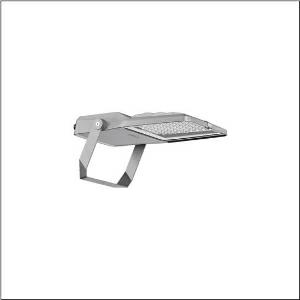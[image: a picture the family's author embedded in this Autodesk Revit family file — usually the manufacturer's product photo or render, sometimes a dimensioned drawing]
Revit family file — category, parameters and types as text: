
# Revit family: floodlight_fl_21_iq_mini___pl64_5xa7772b5e1a_cdb2
name_source: partatom
category: Lighting Fixtures
units: mm (PartAtom-declared; Revit-internal decimal feet)

## family parameters
Cut with Voids When Loaded = No
Host = Face
Light Source = No
Part Type = Normal
Room Calculation Point = No
Round Connector Dimension = Use Diameter
Shared = No

## types (1)
- --- (1 x LED, 5620 lm, 45.5 W, 4000K)
    Apparent Load = 46 VA
    CIE Flux Codes = 28 80 98 100 100
    Color Rendering = 80
    Color Temperature = 4000K
    Default Elevation = 1800 mm
    Description = Floodlight FL 21 iQ mini, floodlight, primary light control with lens, of PMMA, primary optical cover: protective disc, of toughened safety glass, transparent, light distribution: PL64, light emission: direct distribution, installation type: surface-mounted, LED, High Power LED, rated luminous flux: 5.620lm, luminous efficacy: 124lm/W, light colour: 840, colour temperature: 4000K, control gear: iQ Street-Remote/DALI, control: Street-Remote, Auto-Match, Temp-Guard, Night-Set, Smart-Wire, Desk-Remote (wireless, voltage-free reading and setting of iQ features in the workshop via application-optimized NFC function/RFID function), optimised constant luminous flux control (CLO 2.0), with terminal, 6-pole, mains connection: 220..240V, AC, 50/60Hz, start of lifetime: 46W, end of service life: 48W, reduction: 22W, luminaire housing, of diecast aluminium, powder-coated, Siteco® metallic grey (DB 702S), corrosivity category C5 mid according to DIN EN ISO 12944, suitable for swimming pools, chlorine-resistant, sealing non-destructively replaceable, mounting bracket, of steel, galvanised, powder-coated, Siteco® metallic grey (DB 702S), protection rating (complete): IP66, insulation class (complete): insulation class II (safety insulation), certification: CE, ENEC, VDE, protection symbol: D, impact resistance: IK08, permissible operating ambient temperature: -40..+40°C, permissible operating ambient temperature for outdoor applications: -40..+50°C, standard: DIN EN 12944, LABS conformity tested according to VDMA 24364:2018-05, packaging unit: 1 piece

Light Distribution: PL64
    Height = 70 mm
    Lamp = 1 x LED
    Lamp Light Flux = 5620 lm
    Lamp Power = 45.5 W
    Lamp count = 1
    Length = 485 mm
    Luminous efficacy = 124 lm/W
    Manufacturer = Siteco
    ModVariant = No
    Model = 5XA7772B5E1A
    Number of Poles = 1
    OnlyDefault = Yes
    Power Factor = 1
    Product Name = Floodlight FL 21 iQ mini | PL64
    Product group = floodlight | pylon annexe
    ProductGroupID = 6200
    Protection Class = Protection class II
    Protection Degree = IP 66
    RLX_Detail_Level = 1
    RLX_Emergency_Light_Flux = 0 lm
    RLX_Emergency_Type = 0
    RLX_Emergency_Type_DB = No
    RlxData = <blob elided: 96157 chars, md5=961fed58>
    Socket = socket
    Standby Power = 0 W
    System Light Flux = 5620 lm
    System Power = 46 W
    Type Comments = factory setting: luminous flux: 100 % | dim-lin: 254 | 463 mA
    Type Image = l_1006845.jpg
    URL = http://relux.com
    VarID = @adj_166722
    Voltage = 0 V
    Weight = 0.00 kg
    Width = 337 mm

## geometry (parser evidence)
native form markers: Blend x4, Sweep x11
no freeform markers — native parametric forms only
